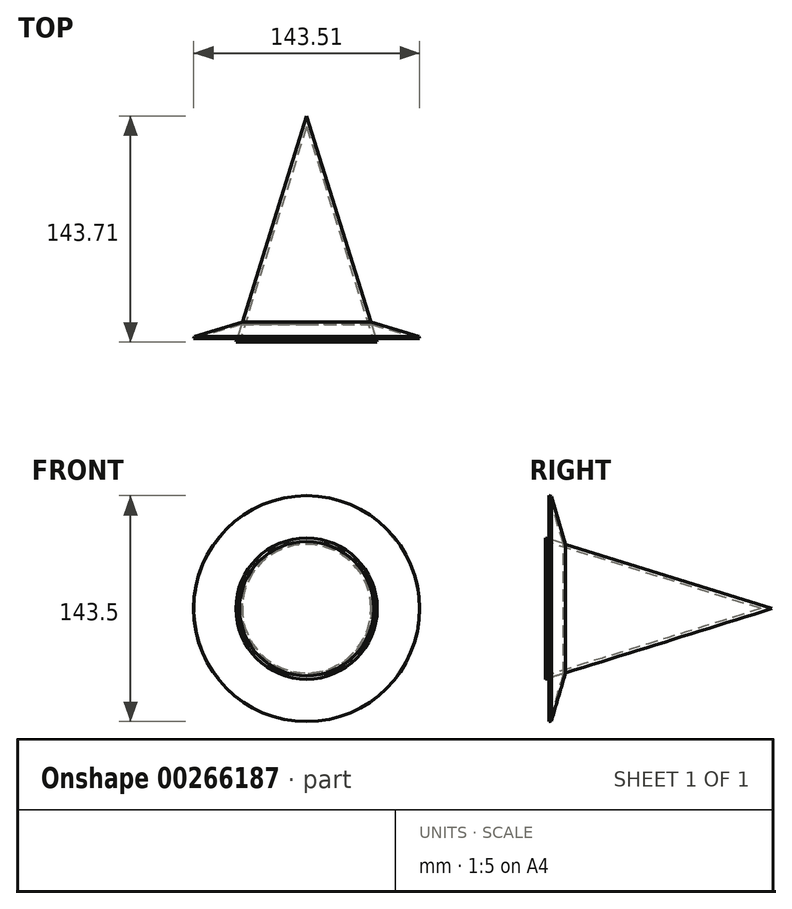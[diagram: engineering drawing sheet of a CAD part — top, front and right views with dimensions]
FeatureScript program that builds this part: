
annotation { "Feature Type Name" : "Feature", "Feature Type Description" : "" }
export const myFeature = defineFeature(function(context is Context, id is Id, definition is map)
    precondition{}
    {
        {
            var Q0;
            Q0=qCreatedBy(makeId("Top.planeOp"),FACE);
            var sketch = newSketch(context, id + "F0", { "sketchPlane" : qUnion([Q0])});
            skLineSegment(sketch, "E0", {"start": v(-135.6, 72.96) * mm, "end": v(-92.93, -63.89) * mm});
            skLineSegment(sketch, "E1.0", {"start": v(-135.6, -63.89) * mm, "end": v(-135.6, 79.82) * mm});
            skLineSegment(sketch, "E1.1", {"start": v(-90.8, -63.89) * mm, "end": v(-135.6, -63.89) * mm});
            skLineSegment(sketch, "E1.2", {"start": v(-135.6, 79.82) * mm, "end": v(-90.8, -63.89) * mm});
            skLineSegment(sketch, "E2", {"start": v(-94.75, -51.19) * mm, "end": v(-64.3, -60.18) * mm});
            skLineSegment(sketch, "E3", {"start": v(-63.85, -61.64) * mm, "end": v(-64.3, -60.18) * mm});
            skLineSegment(sketch, "E4", {"start": v(-63.85, -61.64) * mm, "end": v(-94.3, -52.64) * mm});
            skSolve(sketch);
        }
        {
            var Q0;
            {var subQ0=sQuery(id+"F0.wireOp",EDGE,"E0");Q0=makeQuery(id+"F0.imprint","IMPRINT",FACE,{"disambiguationData":[TD([[makeQuery(id+"F0.imprint","IMPRINT",EDGE,{"derivedFrom":subQ0}),1.0]])]});}
            var Q1;
            {var subQ0=sQuery(id+"F0.wireOp",EDGE,"E2");Q1=makeQuery(id+"F0.imprint","IMPRINT",FACE,{"disambiguationData":[TD([[makeQuery(id+"F0.imprint","IMPRINT",EDGE,{"derivedFrom":subQ0}),-1.0]])]});}
            var Q2;
            Q2=sQuery(id+"F0.wireOp",EDGE,"E1.0");
            revolve(context, id + "F1", {"entities" : qUnion([Q0, Q1]), "axis" : qUnion([Q2]), "revolveType" : RevolveType.FULL});
        }
    });
